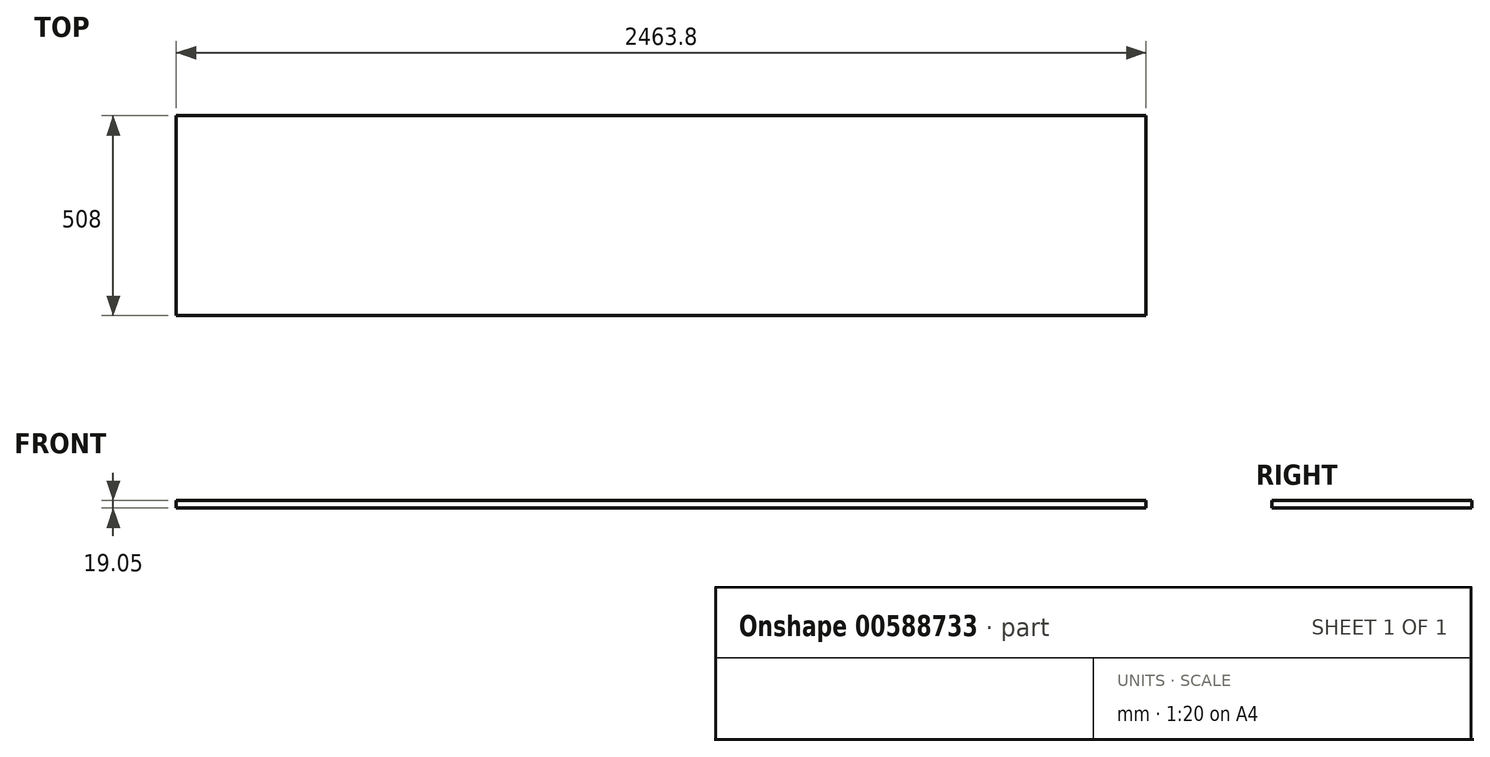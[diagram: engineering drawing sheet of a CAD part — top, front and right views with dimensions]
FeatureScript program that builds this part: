
annotation { "Feature Type Name" : "Feature", "Feature Type Description" : "" }
export const myFeature = defineFeature(function(context is Context, id is Id, definition is map)
    precondition{}
    {
        {
            var Q0;
            Q0=qCreatedBy(makeId("Top.planeOp"),FACE);
            var sketch = newSketch(context, id + "F0", { "sketchPlane" : qUnion([Q0])});
            skLineSegment(sketch, "E0.bottom", {"start": v(1231.9, -254) * mm, "end": v(-1231.9, -254) * mm});
            skLineSegment(sketch, "E0.top", {"start": v(1231.9, 254) * mm, "end": v(-1231.9, 254) * mm});
            skLineSegment(sketch, "E0.left", {"start": v(1231.9, -254) * mm, "end": v(1231.9, 254) * mm});
            skLineSegment(sketch, "E0.right", {"start": v(-1231.9, -254) * mm, "end": v(-1231.9, 254) * mm});
            skPoint(sketch, "E0.middle", {"position": v(0, 0) * mm});
            skSolve(sketch);
        }
        {
            var Q0;
            Q0=makeQuery(id+"F0.imprint","IMPRINT",FACE,{"disambiguationData":[TD([[makeQuery(id+"F0.imprint","IMPRINT",EDGE,{"derivedFrom":sQuery(id+"F0.wireOp",EDGE,"E0.bottom")}),-1.0]])]});
            extrude(context, id + "F1", {"entities" : qUnion([Q0]), "depth" : 19.05 * mm, "offsetDistance" : 25.4 * mm});
        }
    });
